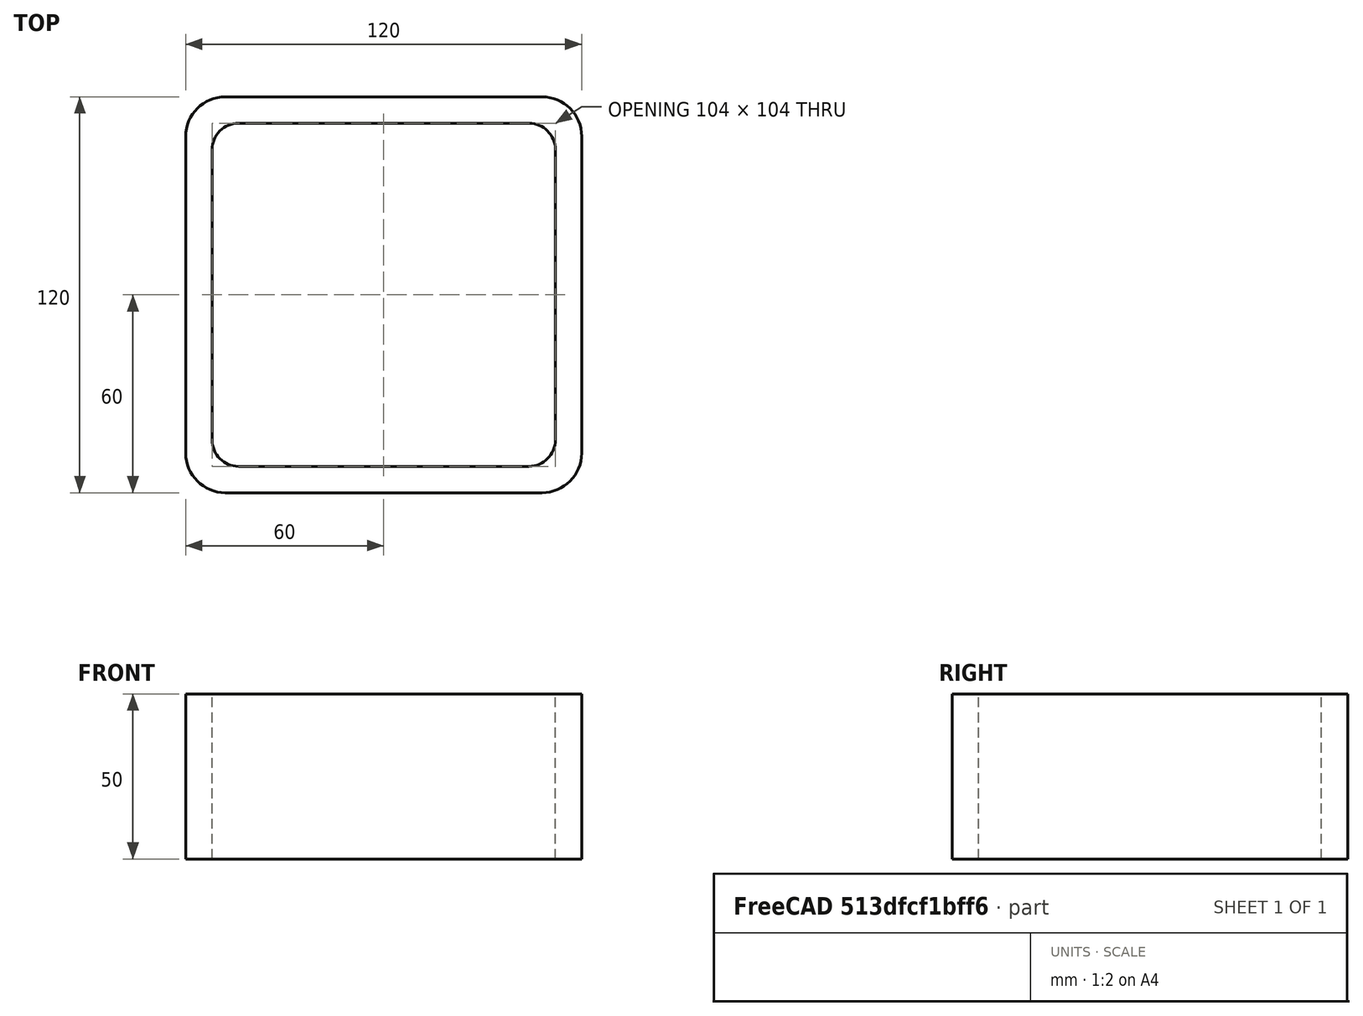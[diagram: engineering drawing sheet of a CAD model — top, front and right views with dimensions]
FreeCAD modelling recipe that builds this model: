
FCSTD DOCUMENT  (FreeCAD 0.15R4671 (Git))
Label: Square hollow section 120x120x8 EN10219 S235JRH
License: All rights reserved
LicenseURL: http://en.wikipedia.org/wiki/All_rights_reserved
objects: Sketcher::SketchObject×1, Part::Extrusion×1
note: 2 computed .brp shape members not serialized (recipe doc carries the construction recipe); baked Part::Feature solids carry a one-line shape summary decoded from their .brp

FEATURE [Sketcher::SketchObject] Sketch
  sketch-geometry (16):
    g0: LineSegment StartX=-44 StartY=52 StartZ=0 EndX=44 EndY=52 EndZ=0
    g1: LineSegment StartX=52 StartY=44 StartZ=0 EndX=52 EndY=-44 EndZ=0
    g2: LineSegment StartX=44 StartY=-52 StartZ=0 EndX=-44 EndY=-52 EndZ=0
    g3: LineSegment StartX=-52 StartY=-44 StartZ=0 EndX=-52 EndY=44 EndZ=0
    g4: LineSegment StartX=-48 StartY=60 StartZ=0 EndX=48 EndY=60 EndZ=0
    g5: LineSegment StartX=60 StartY=48 StartZ=0 EndX=60 EndY=-48 EndZ=0
    g6: LineSegment StartX=48 StartY=-60 StartZ=0 EndX=-48 EndY=-60 EndZ=0
    g7: LineSegment StartX=-60 StartY=-48 StartZ=0 EndX=-60 EndY=48 EndZ=0
    g8: ArcOfCircle CenterX=-44 CenterY=44 CenterZ=0 NormalX=0 NormalY=0 NormalZ=1 Radius=8 StartAngle=1.5708 EndAngle=3.14159
    g9: ArcOfCircle CenterX=44 CenterY=44 CenterZ=0 NormalX=0 NormalY=0 NormalZ=1 Radius=8 StartAngle=0 EndAngle=1.5708
    g10: ArcOfCircle CenterX=44 CenterY=-44 CenterZ=0 NormalX=0 NormalY=0 NormalZ=1 Radius=8 StartAngle=4.71239 EndAngle=6.28319
    g11: ArcOfCircle CenterX=-44 CenterY=-44 CenterZ=0 NormalX=0 NormalY=0 NormalZ=1 Radius=8 StartAngle=3.14159 EndAngle=4.71239
    g12: ArcOfCircle CenterX=48 CenterY=48 CenterZ=0 NormalX=0 NormalY=0 NormalZ=1 Radius=12 StartAngle=0 EndAngle=1.5708
    g13: ArcOfCircle CenterX=48 CenterY=-48 CenterZ=0 NormalX=0 NormalY=0 NormalZ=1 Radius=12 StartAngle=4.71239 EndAngle=6.28319
    g14: ArcOfCircle CenterX=-48 CenterY=-48 CenterZ=0 NormalX=0 NormalY=0 NormalZ=1 Radius=12 StartAngle=3.14159 EndAngle=4.71239
    g15: ArcOfCircle CenterX=-48 CenterY=48 CenterZ=0 NormalX=0 NormalY=0 NormalZ=1 Radius=12 StartAngle=1.5708 EndAngle=3.14159
  constraints (36):
    c: Horizontal(g2)
    c: Vertical(g3)
    c: Horizontal(g6)
    c: Vertical(g7)
    c: Tangent(g3,g8) = 1.5708
    c: Tangent(g0,g8) = 1.5708
    c: Tangent(g0,g9) = 1.5708
    c: Tangent(g1,g9) = 1.5708
    c: Tangent(g1,g10) = 1.5708
    c: Tangent(g2,g10) = 1.5708
    c: Tangent(g2,g11) = 1.5708
    c: Tangent(g3,g11) = 1.5708
    c: Tangent(g4,g12) = 1.5708
    c: Tangent(g5,g12) = 1.5708
    c: Tangent(g5,g13) = 1.5708
    c: Tangent(g6,g13) = 1.5708
    c: Tangent(g6,g14) = 1.5708
    c: Tangent(g7,g14) = 1.5708
    c: Tangent(g7,g15) = 1.5708
    c: Tangent(g4,g15) = 1.5708
    c: Equal(g9,g8)
    c: Equal(g9,g11)
    c: Equal(g9,g10)
    c: Equal(g12,g15)
    c: Equal(g12,g14)
    c: Equal(g12,g13)
    c: Symmetric(g4,g6,g-1)
    c: Symmetric(g7,g5,g-2)
    c: DistanceY(g4,g6) = -120
    c: DistanceX(g7,g5) = 120
    c: Symmetric(g3,g1,g-2)
    c: Symmetric(g0,g2,g-1)
    c: DistanceY(g0,g4) = 8
    c: DistanceX(g5,g1) = -8
    c: Radius(g9) = 8
    c: Radius(g12) = 12
FEATURE [Part::Extrusion] Extrude  label="Square hollow section 120x120x8 EN10219 S235JRH"
  Base = -> Sketch
  Dir = (0,0,50)
  Solid = true
